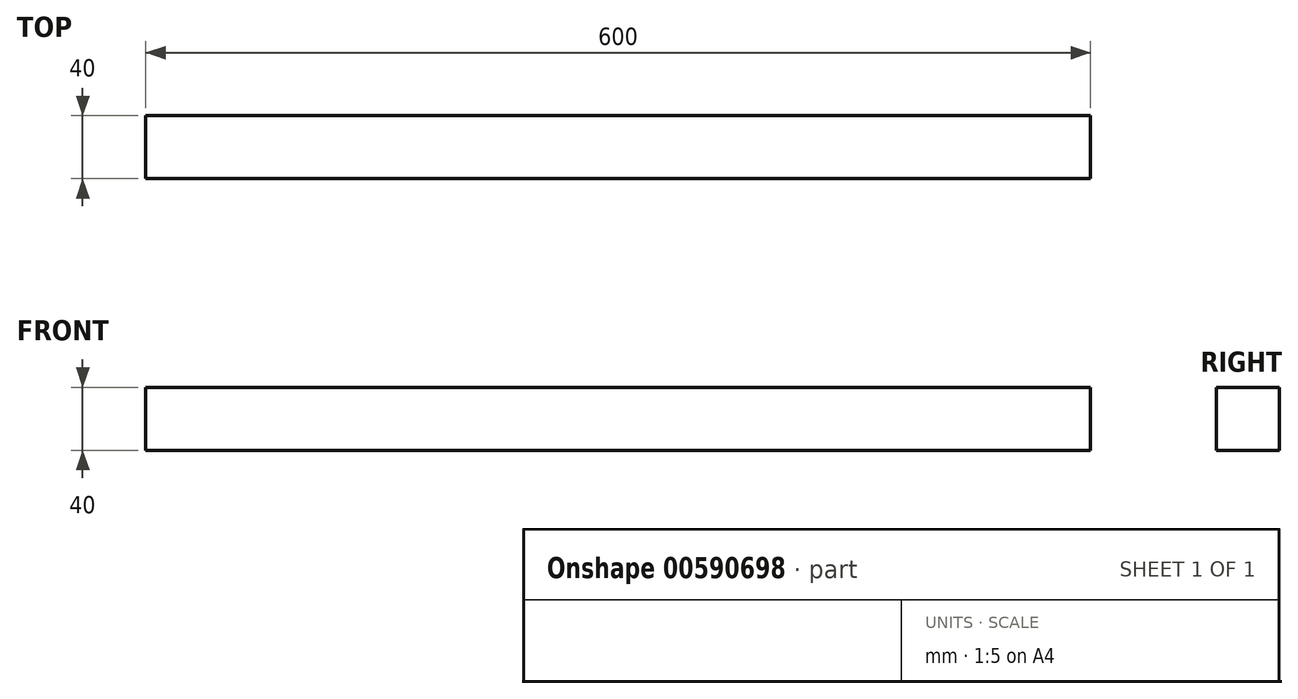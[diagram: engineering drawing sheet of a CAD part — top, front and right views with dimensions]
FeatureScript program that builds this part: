
annotation { "Feature Type Name" : "Feature", "Feature Type Description" : "" }
export const myFeature = defineFeature(function(context is Context, id is Id, definition is map)
    precondition{}
    {
        {
            assignVariable(context, id + "F0", {"name" : "longueur", "anyValue" : 40});
        }
        {
            var Q0;
            Q0=qCreatedBy(makeId("Front.planeOp"),FACE);
            var sketch = newSketch(context, id + "F1", { "sketchPlane" : qUnion([Q0])});
            skLineSegment(sketch, "E0.bottom", {"start": v(-300, 20) * mm, "end": v(300, 20) * mm});
            skLineSegment(sketch, "E0.top", {"start": v(-300, -20) * mm, "end": v(300, -20) * mm});
            skLineSegment(sketch, "E0.left", {"start": v(-300, 20) * mm, "end": v(-300, -20) * mm});
            skLineSegment(sketch, "E0.right", {"start": v(300, 20) * mm, "end": v(300, -20) * mm});
            skPoint(sketch, "E0.middle", {"position": v(0, 0) * mm});
            skSolve(sketch);
        }
        {
            var Q0;
            Q0=qSketchRegion(id+"F1",true);
            extrude(context, id + "F2", {"entities" : qUnion([Q0]), "endBound" : BoundingType.SYMMETRIC, "depth" : (getVariable(context, 'longueur')) * mm, "offsetDistance" : 25 * mm});
        }
    });
